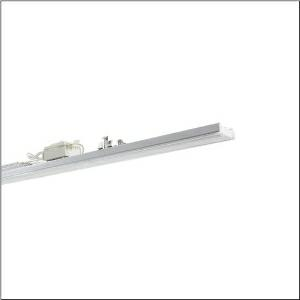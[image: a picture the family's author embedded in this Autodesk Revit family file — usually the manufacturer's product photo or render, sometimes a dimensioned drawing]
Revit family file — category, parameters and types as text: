
# Revit family: licross_21_recessed_ho_52tl12dv4l2md
name_source: partatom
category: Lighting Fixtures
units: mm (PartAtom-declared; Revit-internal decimal feet)

## family parameters
Cut with Voids When Loaded = No
Host = Face
Light Source = No
Part Type = Normal
Room Calculation Point = No
Round Connector Dimension = Use Diameter
Shared = No

## types (1)
- --- (1 x LED, 22710 lm, 125.6 W, 4000K)
    Apparent Load = 126 VA
    CIE Flux Codes = 69 91 98 100 100
    Color Rendering = 80
    Color Temperature = 4000K
    Default Elevation = 1800 mm
    Description = Licross 21 Recessed HO, luminaire insert, of sheet steel, galvanised, coil coated, white, length: 2.250mm, width: 66mm, height: 67mm, LED rated luminous flux: 22.710lm, light colour: 840, SDCM (Standard Deviation of Colour Matching)MacAdam ≤ 3 SDCM (initial), control gear: DALI 2 (for two DALI lines), with plug, 6-pole, with phase selection, mains connection: 220..240V, AC/DC, 0/50..60Hz, rated input power: 126W, without changeover relay, for emergency light function, for central battery installations according to EN 60598-2-22, internal wiring halogen-free, primary optical cover: cover, of PMMA, light emission: direct distribution, primary light characteristic: symmetric, protection rating (complete): IP40, insulation class (complete): insulation class I (protective earthing), certification: CE, ENEC, VDE, UKCA, protection symbol: D if used in an environment without relevant dust loads with corresponding accessories, impact resistance: IK06, permissible ambient temperature for indoor applications: -40..+30°C, standard: EN 60598-2-22, corresponds to IFS (International Featured Standards) requirements for safety and quality in the food industry, reducing of maximum allowable ambient temperature of 5°C with ceiling mounting, LABS conformity tested according to VDMA 24364:2018-05, The light source and the operating device comply with the requirements of the Ecodesign Regulation (EU) 2019/2020 and are replaceable in accordance with this regulation, packaging unit: 1 piece
    Height = 58 mm
    Lamp = 1 x LED
    Lamp Light Flux = 22710 lm
    Lamp Power = 125.6 W
    Lamp count = 1
    Length = 2250 mm
    Luminous efficacy = 181 lm/W
    Manufacturer = Siteco
    ModVariant = No
    Model = 52TL12DV4L2MD
    Mounting Place = Ceiling
    Mounting Type = Pendant
    Number of Poles = 1
    OnlyDefault = Yes
    Power Factor = 1
    Product Name = Licross 21 Recessed HO
    Product group = luminaire insert | ceiling pendant
    ProductGroupID = 901
    Protection Class = Protection class I
    Protection Degree = IP 40
    RLX_Detail_Level = 1
    RLX_Emergency_Light_Flux = 0 lm
    RLX_Emergency_Type = 0
    RLX_Emergency_Type_DB = No
    RlxData = <blob elided: 30133 chars, md5=576220f6>
    Socket = socket
    Standby Power = 0 W
    System Light Flux = 22710 lm
    System Power = 126 W
    Type Comments = : AC-mode, luminous flux: 100 % | dim-lin: 254 | 489 mA
    Type Image = l_1296930.jpg
    URL = http://relux.com
    VarID = @adj_111671
    Voltage = 0 V
    Weight = 0.00 kg
    Width = 66 mm

## geometry (parser evidence)
native form markers: Blend x4, Sweep x10
no freeform markers — native parametric forms only
